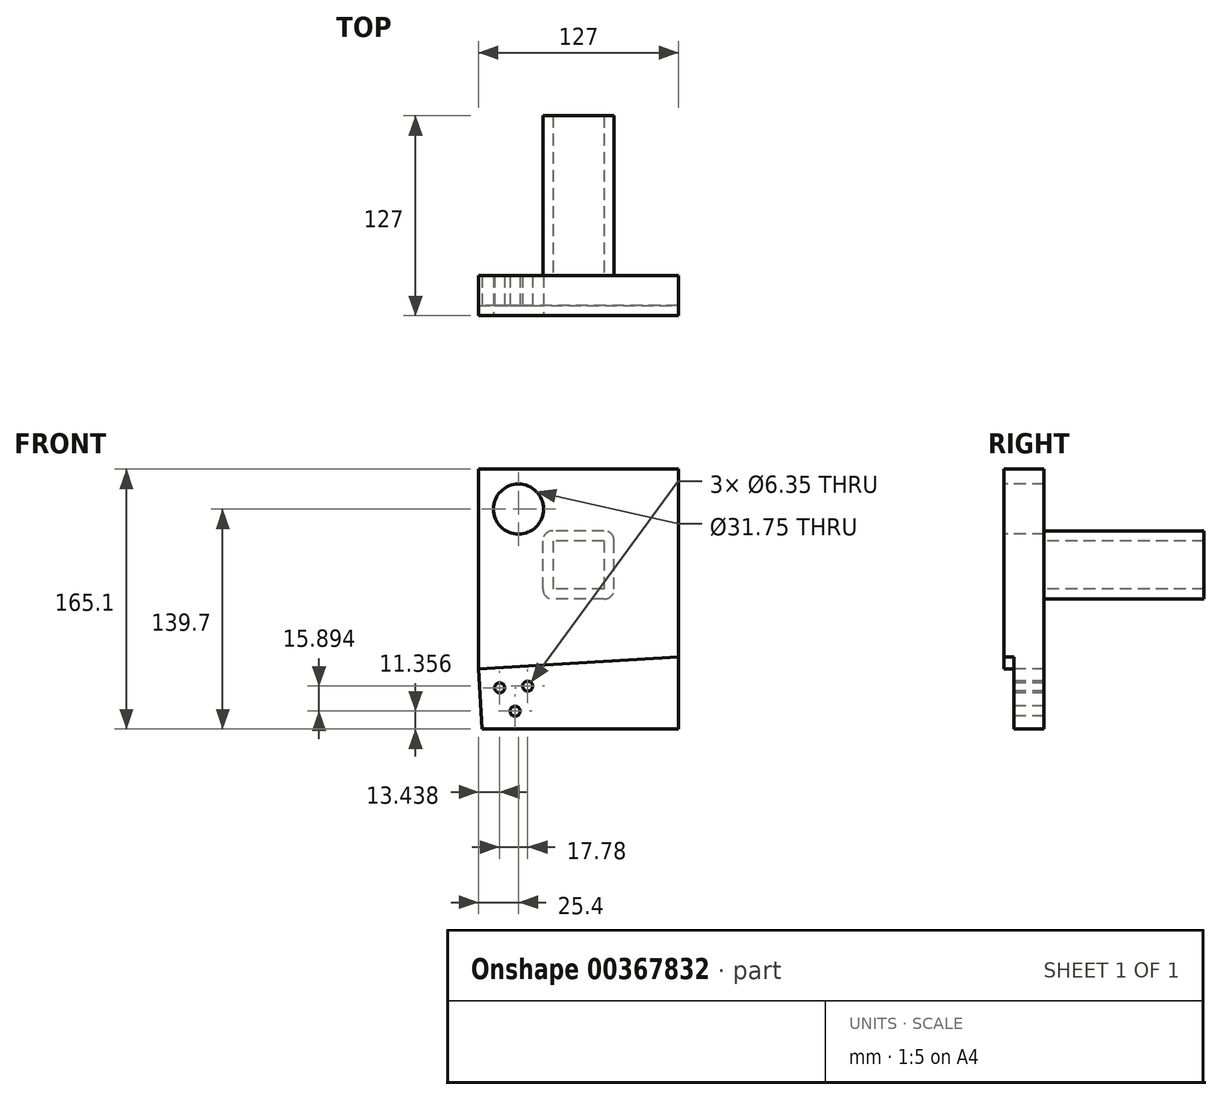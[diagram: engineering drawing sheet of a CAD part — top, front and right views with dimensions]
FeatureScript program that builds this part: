
annotation { "Feature Type Name" : "Feature", "Feature Type Description" : "" }
export const myFeature = defineFeature(function(context is Context, id is Id, definition is map)
    precondition{}
    {
        {
            var Q0;
            Q0=qCreatedBy(makeId("Front.planeOp"),FACE);
            var sketch = newSketch(context, id + "F0", { "sketchPlane" : qUnion([Q0])});
            skLineSegment(sketch, "E0.bottom", {"start": v(63.5, 82.55) * mm, "end": v(-63.5, 82.55) * mm});
            skLineSegment(sketch, "E0.top", {"start": v(63.5, -82.55) * mm, "end": v(-63.5, -82.55) * mm});
            skLineSegment(sketch, "E0.left", {"start": v(63.5, 82.55) * mm, "end": v(63.5, -82.55) * mm});
            skLineSegment(sketch, "E0.right", {"start": v(-63.5, 82.55) * mm, "end": v(-63.5, -82.55) * mm});
            skPoint(sketch, "E0.middle", {"position": v(0, 0) * mm});
            skCircle(sketch, "E1", {"center": v(-38.1, 57.15) * mm, "radius": 15.88 * mm});
            skSolve(sketch);
        }
        {
            var Q0;
            Q0 = qSketchRegion(id + "F0", true);
            extrude(context, id + "F1", {"entities" : qUnion([Q0]), "oppositeDirection" : true, "depth" : 25.4 * mm});
        }
        {
            var Q0;
            Q0=makeQuery(id+"F1.opExtrude","CAP_FACE",FACE,{"disambiguationData":[OSD([sQuery(id+"F0.wireOp",EDGE,"E0.bottom"),sQuery(id+"F0.wireOp",EDGE,"E0.top"),sQuery(id+"F0.wireOp",EDGE,"E0.left"),sQuery(id+"F0.wireOp",EDGE,"E0.right"),sQuery(id+"F0.wireOp",EDGE,"E1")])],"isStart":true});
            var sketch = newSketch(context, id + "F2", { "sketchPlane" : qUnion([Q0])});
            skLineSegment(sketch, "E2", {"start": v(-63.5, -44.45) * mm, "end": v(63.5, -36.83) * mm});
            skLineSegment(sketch, "E3", {"start": v(-63.5, -44.45) * mm, "end": v(-61.21, -82.55) * mm, "construction": true});
            skCircle(sketch, "E4", {"center": v(-50.06, -56.37) * mm, "radius": 3.18 * mm});
            skLineSegment(sketch, "E5", {"start": v(-50.06, -56.37) * mm, "end": v(-13.58, -54.18) * mm, "construction": true});
            skCircle(sketch, "E6", {"center": v(-32.28, -55.3) * mm, "radius": 3.18 * mm});
            skCircle(sketch, "E7", {"center": v(-40.25, -71.2) * mm, "radius": 3.18 * mm});
            skSolve(sketch);
        }
        {
            var Q0;
            Q0 = qSketchRegion(id + "F2", true);
            var Q1;
            {var subQ0=sQuery(id+"F2.wireOp",EDGE,"E2");Q1=makeQuery(id+"F2.imprint","IMPRINT",FACE,{"disambiguationData":[TD([[makeQuery(id+"F2.imprint","IMPRINT",EDGE,{"derivedFrom":subQ0}),-1.0]])]});}
            extrude(context, id + "F3", {"entities" : qUnion([Q0, Q1]), "operationType" : NewBodyOperationType.REMOVE, "oppositeDirection" : true, "depth" : 6.35 * mm});
        }
        {
            var Q0;
            Q0 = qSketchRegion(id + "F2", true);
            extrude(context, id + "F4", {"entities" : qUnion([Q0]), "operationType" : NewBodyOperationType.REMOVE, "oppositeDirection" : true, "depth" : 25.4 * mm});
        }
        {
            var Q0;
            Q0=makeQuery(id+"F3.boolean.opBoolean","COPY",FACE,{"derivedFrom":makeQuery(id+"F3.opExtrude","CAP_FACE",FACE,{"disambiguationData":[OSD([sQuery(id+"F0.wireOp",EDGE,"E0.top"),sQuery(id+"F0.wireOp",EDGE,"E0.left"),sQuery(id+"F0.wireOp",EDGE,"E0.right"),sQuery(id+"F2.wireOp",EDGE,"E2")])],"isStart":false})});
            var sketch = newSketch(context, id + "F5", { "sketchPlane" : qUnion([Q0])});
            skLineSegment(sketch, "E8", {"start": v(-63.5, -44.45) * mm, "end": v(-61.21, -82.55) * mm});
            skSolve(sketch);
        }
        {
            var Q0;
            {var subQ0=sQuery(id+"F5.wireOp",EDGE,"E8");Q0=makeQuery(id+"F5.imprint","IMPRINT",FACE,{"disambiguationData":[TD([[makeQuery(id+"F5.imprint","IMPRINT",EDGE,{"derivedFrom":subQ0}),-1.0]])]});}
            extrude(context, id + "F6", {"entities" : qUnion([Q0]), "operationType" : NewBodyOperationType.REMOVE, "oppositeDirection" : true, "depth" : 25.4 * mm});
        }
        {
            var Q0;
            Q0=makeQuery(id+"F1.opExtrude","CAP_FACE",FACE,{"disambiguationData":[OSD([sQuery(id+"F0.wireOp",EDGE,"E0.bottom"),sQuery(id+"F0.wireOp",EDGE,"E0.top"),sQuery(id+"F0.wireOp",EDGE,"E0.left"),sQuery(id+"F0.wireOp",EDGE,"E0.right"),sQuery(id+"F0.wireOp",EDGE,"E1")])],"isStart":true});
            var sketch = newSketch(context, id + "F7", { "sketchPlane" : qUnion([Q0])});
            skLineSegment(sketch, "E9.bottom", {"start": v(16.26, 0) * mm, "end": v(-16.26, 0) * mm});
            skLineSegment(sketch, "E9.top", {"start": v(16.26, 43.38) * mm, "end": v(-16.26, 43.38) * mm});
            skLineSegment(sketch, "E9.left", {"start": v(22.6, 6.35) * mm, "end": v(22.6, 37.03) * mm});
            skLineSegment(sketch, "E9.right", {"start": v(-22.6, 6.35) * mm, "end": v(-22.6, 37.03) * mm});
            skPoint(sketch, "E9.middle", {"position": v(0, 21.7) * mm});
            skPoint(sketch, "E10.visualSharp", {"position": v(-22.6, 43.38) * mm});
            skArc(sketch, "E10.filletArc", {"start": v(-16.26, 43.38) * mm, "mid": v(-20.75, 41.52) * mm, "end": v(-22.6, 37.03) * mm});
            skPoint(sketch, "E11.visualSharp", {"position": v(22.6, 43.38) * mm});
            skArc(sketch, "E11.filletArc", {"start": v(22.6, 37.03) * mm, "mid": v(20.75, 41.52) * mm, "end": v(16.26, 43.38) * mm});
            skPoint(sketch, "E12.visualSharp", {"position": v(22.6, 0) * mm});
            skArc(sketch, "E12.filletArc", {"start": v(16.26, 0) * mm, "mid": v(20.75, 1.86) * mm, "end": v(22.6, 6.35) * mm});
            skPoint(sketch, "E13.visualSharp", {"position": v(-22.6, 0) * mm});
            skArc(sketch, "E13.filletArc", {"start": v(-22.6, 6.35) * mm, "mid": v(-20.75, 1.86) * mm, "end": v(-16.26, 0) * mm});
            skLineSegment(sketch, "E14.bottom", {"start": v(16.26, 37.03) * mm, "end": v(-16.26, 37.03) * mm});
            skLineSegment(sketch, "E14.top", {"start": v(16.26, 6.35) * mm, "end": v(-16.26, 6.35) * mm});
            skLineSegment(sketch, "E14.left", {"start": v(16.26, 37.03) * mm, "end": v(16.26, 6.35) * mm});
            skLineSegment(sketch, "E14.right", {"start": v(-16.26, 37.03) * mm, "end": v(-16.26, 6.35) * mm});
            skSolve(sketch);
        }
        {
            var Q0;
            Q0=makeQuery(id+"F7.imprint","IMPRINT",FACE,{"disambiguationData":[TD([[makeQuery(id+"F7.imprint","IMPRINT",EDGE,{"derivedFrom":sQuery(id+"F7.wireOp",EDGE,"E9.bottom")}),-1.0]])]});
            extrude(context, id + "F8", {"entities" : qUnion([Q0]), "operationType" : NewBodyOperationType.ADD, "oppositeDirection" : true, "depth" : 127 * mm});
        }
    });
